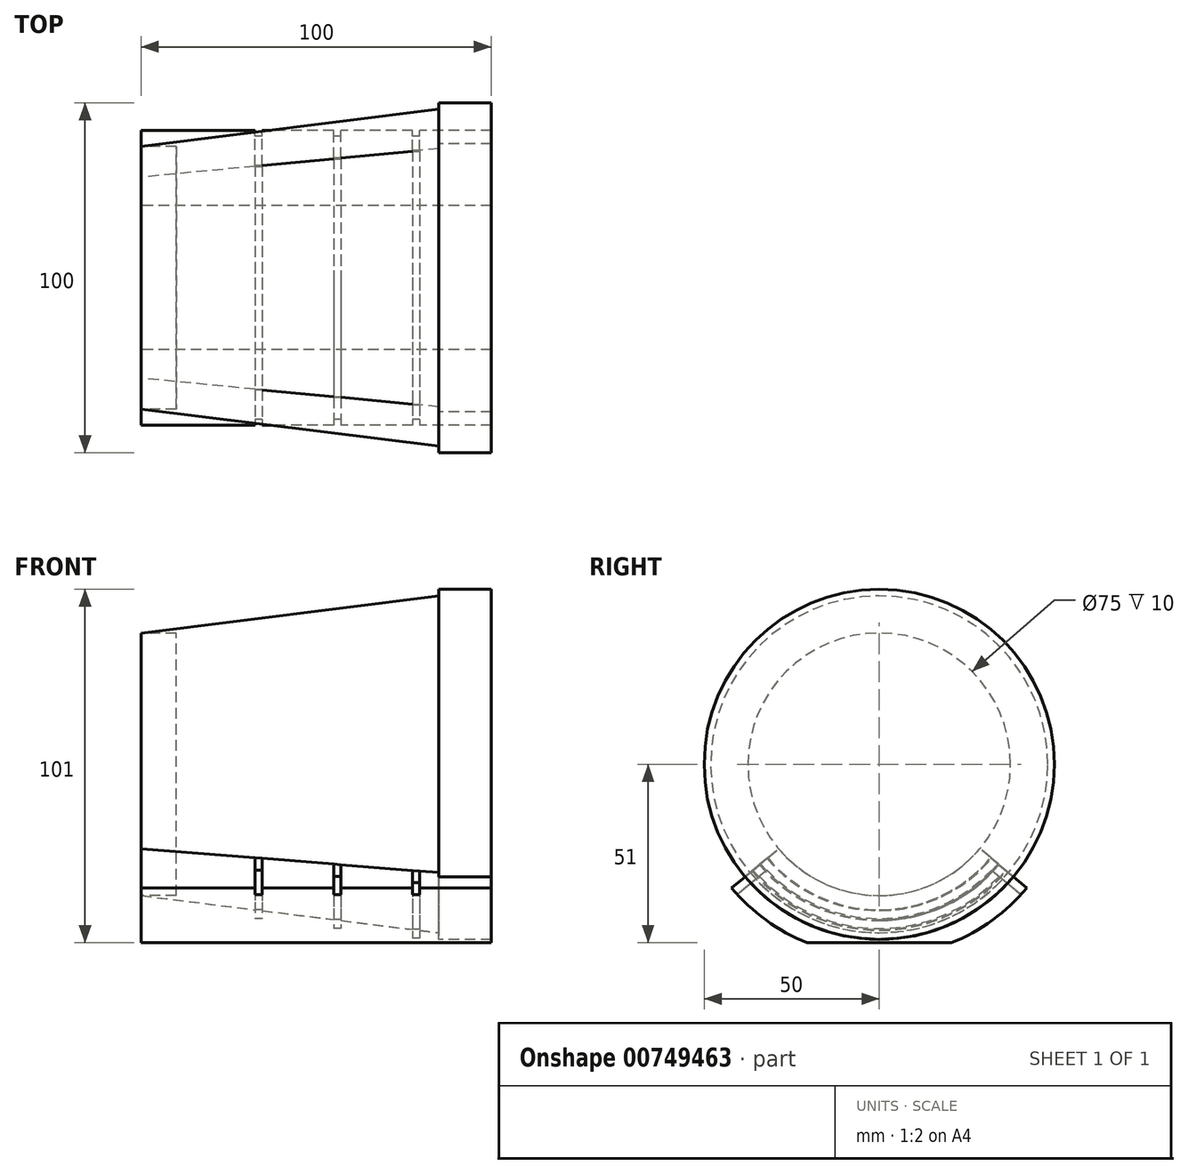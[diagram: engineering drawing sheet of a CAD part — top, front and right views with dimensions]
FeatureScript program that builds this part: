
annotation { "Feature Type Name" : "Feature", "Feature Type Description" : "" }
export const myFeature = defineFeature(function(context is Context, id is Id, definition is map)
    precondition{}
    {
        {
            var Q0;
            Q0=qCreatedBy(makeId("Right.planeOp"),FACE);
            var sketch = newSketch(context, id + "F0", { "sketchPlane" : qUnion([Q0])});
            skCircle(sketch, "E0", {"center": v(0, 0) * mm, "radius": 37.5 * mm});
            skSolve(sketch);
        }
        {
            var Q0;
            Q0=makeQuery(id+"F0.imprint","IMPRINT",FACE,{"disambiguationData":[TD([[makeQuery(id+"F0.imprint","IMPRINT",EDGE,{"derivedFrom":sQuery(id+"F0.wireOp",EDGE,"E0")}),1.0]])]});
            cPlane(context, id + "F1", {"entities" : qUnion([Q0]), "cplaneType" : CPlaneType.OFFSET, "offset" : 100 * mm, "width" : 150 * mm, "height" : 150 * mm});
        }
        {
            var Q0;
            Q0=qCreatedBy(id+"F1.planeOp",FACE);
            var sketch = newSketch(context, id + "F2", { "sketchPlane" : qUnion([Q0])});
            skCircle(sketch, "E1", {"center": v(0, 0) * mm, "radius": 50 * mm});
            skSolve(sketch);
        }
        {
            var Q0;
            Q0=qCreatedBy(id+"F1.planeOp",FACE);
            cPlane(context, id + "F3", {"entities" : qUnion([Q0]), "cplaneType" : CPlaneType.OFFSET, "offset" : 15 * mm, "oppositeDirection" : true, "width" : 150 * mm, "height" : 150 * mm});
        }
        {
            var Q0;
            Q0=qCreatedBy(id+"F3.planeOp",FACE);
            var sketch = newSketch(context, id + "F4", { "sketchPlane" : qUnion([Q0])});
            skCircle(sketch, "E2.0", {"center": v(0, 0) * mm, "radius": 50 * mm});
            skSolve(sketch);
        }
        {
            var Q0;
            Q0=makeQuery(id+"F0.imprint","IMPRINT",FACE,{"disambiguationData":[TD([[makeQuery(id+"F0.imprint","IMPRINT",EDGE,{"derivedFrom":sQuery(id+"F0.wireOp",EDGE,"E0")}),1.0]])]});
            var Q1;
            Q1=makeQuery(id+"F2.imprint","IMPRINT",FACE,{"disambiguationData":[TD([[makeQuery(id+"F2.imprint","IMPRINT",EDGE,{"derivedFrom":sQuery(id+"F2.wireOp",EDGE,"E1")}),1.0]])]});
            loft(context, id + "F5", {"sheetProfilesArray" : [{ "sheetProfileEntities" : qUnion([Q0]) }, { "sheetProfileEntities" : qUnion([Q1]) }]});
        }
        {
            var Q0;
            Q0=makeQuery(id+"F4.imprint","IMPRINT",FACE,{"disambiguationData":[TD([[makeQuery(id+"F4.imprint","IMPRINT",EDGE,{"derivedFrom":sQuery(id+"F4.wireOp",EDGE,"E2.0")}),1.0]])]});
            var Q1;
            Q1=makeQuery(id+"F5.opLoft","CAP_FACE",FACE,{"disambiguationData":[OSD([makeQuery(id+"F2.imprint","IMPRINT",FACE,{"disambiguationData":[TD([[makeQuery(id+"F2.imprint","IMPRINT",EDGE,{"derivedFrom":sQuery(id+"F2.wireOp",EDGE,"E1")}),1.0]])]})])],"isStart":true});
            extrude(context, id + "F6", {"entities" : qUnion([Q0]), "operationType" : NewBodyOperationType.ADD, "endBound" : BoundingType.UP_TO_SURFACE, "depth" : 25 * mm, "endBoundEntityFace" : qUnion([Q1]), "offsetDistance" : 25 * mm});
        }
        {
            var Q0;
            Q0=makeQuery(id+"F5.opLoft","CAP_FACE",FACE,{"disambiguationData":[OSD([makeQuery(id+"F0.imprint","IMPRINT",FACE,{"disambiguationData":[TD([[makeQuery(id+"F0.imprint","IMPRINT",EDGE,{"derivedFrom":sQuery(id+"F0.wireOp",EDGE,"E0")}),1.0]])]})])],"isStart":true});
            extrude(context, id + "F7", {"entities" : qUnion([Q0]), "operationType" : NewBodyOperationType.REMOVE, "oppositeDirection" : true, "depth" : 10 * mm, "offsetDistance" : 25 * mm});
        }
        {
            var Q0;
            Q0=qCreatedBy(makeId("Front.planeOp"),FACE);
            var sketch = newSketch(context, id + "F8", { "sketchPlane" : qUnion([Q0])});
            skLineSegment(sketch, "E3", {"start": v(85, -48.13) * mm, "end": v(0, -37.5) * mm});
            skLineSegment(sketch, "E4", {"start": v(100, -50) * mm, "end": v(85, -50) * mm});
            skLineSegment(sketch, "E5.0", {"start": v(85, -48.13) * mm, "end": v(85, -50) * mm});
            skLineSegment(sketch, "E6.0", {"start": v(100, -48.13) * mm, "end": v(100, -50) * mm});
            skPoint(sketch, "E7.orphan", {"position": v(85, 50) * mm});
            skPoint(sketch, "E8", {"position": v(100, -48.13) * mm});
            skPoint(sketch, "E9.orphan", {"position": v(100, 50) * mm});
            skLineSegment(sketch, "E10", {"start": v(100, -50) * mm, "end": v(100, -55) * mm});
            skLineSegment(sketch, "E11", {"start": v(100, -55) * mm, "end": v(0, -55) * mm});
            skLineSegment(sketch, "E12", {"start": v(0, -55) * mm, "end": v(0, -37.5) * mm});
            skLineSegment(sketch, "E13", {"start": v(0, 0) * mm, "end": v(107.52, 0) * mm, "construction": true});
            skSolve(sketch);
        }
        {
            var Q0;
            Q0=makeQuery(id+"F8.imprint","IMPRINT",FACE,{"disambiguationData":[TD([[makeQuery(id+"F8.imprint","IMPRINT",EDGE,{"derivedFrom":sQuery(id+"F8.wireOp",EDGE,"E3")}),1.0]])]});
            var Q1;
            Q1=sQuery(id+"F8.wireOp",EDGE,"E13");
            revolve(context, id + "F9", {"surfaceOperationType" : NewSurfaceOperationType.NEW, "entities" : qUnion([Q0]), "axis" : qUnion([Q1]), "revolveType" : RevolveType.SYMMETRIC, "angle" : 100 * degree});
        }
        {
            var Q0;
            Q0=makeQuery(id+"F9.opRevolve","CAP_FACE",FACE,{"disambiguationData":[OSD([sQuery(id+"F8.wireOp",EDGE,"E3"),sQuery(id+"F8.wireOp",EDGE,"E4"),sQuery(id+"F8.wireOp",EDGE,"E5.0"),sQuery(id+"F8.wireOp",EDGE,"E10"),sQuery(id+"F8.wireOp",EDGE,"E11"),sQuery(id+"F8.wireOp",EDGE,"E12")])],"isStart":true});
            var sketch = newSketch(context, id + "F10", { "sketchPlane" : qUnion([Q0])});
            skLineSegment(sketch, "E14.bottom", {"start": v(32.5, -41.56) * mm, "end": v(34.5, -41.56) * mm});
            skLineSegment(sketch, "E14.top", {"start": v(32.5, -44.06) * mm, "end": v(34.5, -44.06) * mm});
            skLineSegment(sketch, "E14.left", {"start": v(32.5, -41.56) * mm, "end": v(32.5, -44.06) * mm});
            skLineSegment(sketch, "E14.right", {"start": v(34.5, -41.56) * mm, "end": v(34.5, -44.06) * mm});
            skLineSegment(sketch, "E15.bottom", {"start": v(55, -44.38) * mm, "end": v(57, -44.38) * mm});
            skLineSegment(sketch, "E15.top", {"start": v(55, -46.88) * mm, "end": v(57, -46.88) * mm});
            skLineSegment(sketch, "E15.left", {"start": v(55, -44.38) * mm, "end": v(55, -46.88) * mm});
            skLineSegment(sketch, "E15.right", {"start": v(57, -44.38) * mm, "end": v(57, -46.88) * mm});
            skLineSegment(sketch, "E16.bottom", {"start": v(77.5, -47.19) * mm, "end": v(79.5, -47.19) * mm});
            skLineSegment(sketch, "E16.top", {"start": v(77.5, -49.69) * mm, "end": v(79.5, -49.69) * mm});
            skLineSegment(sketch, "E16.left", {"start": v(77.5, -47.19) * mm, "end": v(77.5, -49.69) * mm});
            skLineSegment(sketch, "E16.right", {"start": v(79.5, -47.19) * mm, "end": v(79.5, -49.69) * mm});
            skSolve(sketch);
        }
        {
            var Q0;
            Q0 = qSketchRegion(id + "F10", true);
            var Q1;
            {var subQ0=sQuery(id+"F10.wireOp",EDGE,"MtueOWO8-KjEm-FWS7-cRDt-SSEm0pxepaqH");Q1=makeQuery(id+"F10.imprint","IMPRINT",FACE,{"disambiguationData":[TD([[makeQuery(id+"F10.imprint","IMPRINT",EDGE,{"derivedFrom":subQ0}),1.0]])]});}
            var Q2;
            {var subQ0=sQuery(id+"F10.wireOp",EDGE,"r30qupwk-UPxA-5DJF-4wcs-cAvNlDd5E6xW");Q2=makeQuery(id+"F10.imprint","IMPRINT",FACE,{"disambiguationData":[TD([[makeQuery(id+"F10.imprint","IMPRINT",EDGE,{"derivedFrom":subQ0}),1.0]])]});}
            var Q3;
            Q3=sQuery(id+"F8.wireOp",EDGE,"E13");
            revolve(context, id + "F11", {"operationType" : NewBodyOperationType.REMOVE, "surfaceOperationType" : NewSurfaceOperationType.NEW, "entities" : qUnion([Q0, Q1, Q2]), "axis" : qUnion([Q3]), "revolveType" : RevolveType.ONE_DIRECTION, "angle" : 100 * degree});
        }
        {
            var Q0;
            Q0=makeQuery(id+"F9.opRevolve","SWEPT_FACE",FACE,{"disambiguationData":[OSD([sQuery(id+"F8.wireOp",EDGE,"E10")])]});
            var sketch = newSketch(context, id + "F12", { "sketchPlane" : qUnion([Q0])});
            skLineSegment(sketch, "E17", {"start": v(0, -50) * mm, "end": v(0, -51) * mm, "construction": true});
            skLineSegment(sketch, "E18", {"start": v(-50.55, -51) * mm, "end": v(49.92, -51) * mm});
            skLineSegment(sketch, "E19", {"start": v(49.92, -51) * mm, "end": v(49.92, -60) * mm});
            skLineSegment(sketch, "E20", {"start": v(49.92, -60) * mm, "end": v(-50.55, -60) * mm});
            skLineSegment(sketch, "E21", {"start": v(-50.55, -60) * mm, "end": v(-50.55, -51) * mm});
            skSolve(sketch);
        }
        {
            var Q0;
            {var subQ0=sQuery(id+"F12.wireOp",EDGE,"E19");Q0=makeQuery(id+"F12.imprint","IMPRINT",FACE,{"disambiguationData":[TD([[makeQuery(id+"F12.imprint","IMPRINT",EDGE,{"derivedFrom":subQ0}),-1.0]])]});}
            var Q1;
            {var subQ0=sQuery(id+"F12.wireOp",EDGE,"E18");var subQ1=makeQuery(id+"F9.opRevolve","SWEPT_EDGE",EDGE,{"disambiguationData":[OSD([sQuery(id+"F8.wireOp",EDGE,"E10"),sQuery(id+"F8.wireOp",EDGE,"E11")])]});var subQ2=makeQuery(id+"F12.imprint","INTERSECT",VERTEX,{"disambiguationData":[OD(0.0)],"derivedFrom":[subQ1,subQ0]});Q1=makeQuery(id+"F12.imprint","IMPRINT",FACE,{"disambiguationData":[TD([[makeQuery(id+"F12.imprint","IMPRINT",EDGE,{"disambiguationData":[TD([[subQ2,-1.0]])],"derivedFrom":subQ0}),-1.0]])]});}
            var Q2;
            Q2=makeQuery(id+"F9.opRevolve","SWEPT_FACE",FACE,{"disambiguationData":[OSD([sQuery(id+"F8.wireOp",EDGE,"E12")])]});
            extrude(context, id + "F13", {"entities" : qUnion([Q0, Q1]), "operationType" : NewBodyOperationType.REMOVE, "endBound" : BoundingType.UP_TO_SURFACE, "oppositeDirection" : true, "depth" : 25 * mm, "endBoundEntityFace" : qUnion([Q2]), "offsetDistance" : 25 * mm});
        }
        {
            var Q0;
            Q0=makeQuery(id+"F9.opRevolve","CAP_FACE",FACE,{"disambiguationData":[OSD([sQuery(id+"F8.wireOp",EDGE,"E3"),sQuery(id+"F8.wireOp",EDGE,"E4"),sQuery(id+"F8.wireOp",EDGE,"E5.0"),sQuery(id+"F8.wireOp",EDGE,"E10"),sQuery(id+"F8.wireOp",EDGE,"E11"),sQuery(id+"F8.wireOp",EDGE,"E12")])],"isStart":true});
            var sketch = newSketch(context, id + "F14", { "sketchPlane" : qUnion([Q0])});
            skLineSegment(sketch, "E22.bottom", {"start": v(32.5, -41.56) * mm, "end": v(34.5, -41.56) * mm});
            skLineSegment(sketch, "E22.top", {"start": v(32.5, -55) * mm, "end": v(34.5, -55) * mm});
            skLineSegment(sketch, "E22.left", {"start": v(32.5, -41.56) * mm, "end": v(32.5, -55) * mm});
            skLineSegment(sketch, "E22.right", {"start": v(34.5, -41.56) * mm, "end": v(34.5, -55) * mm});
            skLineSegment(sketch, "E23.bottom", {"start": v(55, -44.38) * mm, "end": v(57, -44.38) * mm});
            skLineSegment(sketch, "E23.top", {"start": v(55, -55) * mm, "end": v(57, -55) * mm});
            skLineSegment(sketch, "E23.left", {"start": v(55, -44.38) * mm, "end": v(55, -55) * mm});
            skLineSegment(sketch, "E23.right", {"start": v(57, -44.38) * mm, "end": v(57, -55) * mm});
            skLineSegment(sketch, "E24.bottom", {"start": v(77.5, -47.19) * mm, "end": v(79.5, -47.19) * mm});
            skLineSegment(sketch, "E24.top", {"start": v(77.5, -55) * mm, "end": v(79.5, -55) * mm});
            skLineSegment(sketch, "E24.left", {"start": v(77.5, -47.19) * mm, "end": v(77.5, -55) * mm});
            skLineSegment(sketch, "E24.right", {"start": v(79.5, -47.19) * mm, "end": v(79.5, -55) * mm});
            skSolve(sketch);
        }
        {
            var Q0;
            {var subQ0=sQuery(id+"F14.wireOp",EDGE,"E22.top");Q0=makeQuery(id+"F14.imprint","IMPRINT",FACE,{"disambiguationData":[TD([[makeQuery(id+"F14.imprint","IMPRINT",EDGE,{"derivedFrom":subQ0}),-1.0]])]});}
            var Q1;
            {var subQ8=sQuery(id+"F14.wireOp",EDGE,"E22.bottom");Q1=makeQuery(id+"F14.imprint","IMPRINT",FACE,{"disambiguationData":[TD([[makeQuery(id+"F14.imprint","IMPRINT",EDGE,{"derivedFrom":subQ8}),-1.0]])]});}
            var Q2;
            {var subQ7=sQuery(id+"F14.wireOp",EDGE,"E23.bottom");Q2=makeQuery(id+"F14.imprint","IMPRINT",FACE,{"disambiguationData":[TD([[makeQuery(id+"F14.imprint","IMPRINT",EDGE,{"derivedFrom":subQ7}),-1.0]])]});}
            var Q3;
            {var subQ0=sQuery(id+"F14.wireOp",EDGE,"E23.top");Q3=makeQuery(id+"F14.imprint","IMPRINT",FACE,{"disambiguationData":[TD([[makeQuery(id+"F14.imprint","IMPRINT",EDGE,{"derivedFrom":subQ0}),-1.0]])]});}
            var Q4;
            {var subQ8=sQuery(id+"F14.wireOp",EDGE,"E24.bottom");Q4=makeQuery(id+"F14.imprint","IMPRINT",FACE,{"disambiguationData":[TD([[makeQuery(id+"F14.imprint","IMPRINT",EDGE,{"derivedFrom":subQ8}),-1.0]])]});}
            var Q5;
            {var subQ0=sQuery(id+"F14.wireOp",EDGE,"E24.top");Q5=makeQuery(id+"F14.imprint","IMPRINT",FACE,{"disambiguationData":[TD([[makeQuery(id+"F14.imprint","IMPRINT",EDGE,{"derivedFrom":subQ0}),-1.0]])]});}
            extrude(context, id + "F15", {"entities" : qUnion([Q0, Q1, Q2, Q3, Q4, Q5]), "operationType" : NewBodyOperationType.REMOVE, "oppositeDirection" : true, "depth" : 2.5 * mm, "offsetDistance" : 25 * mm});
        }
        {
            var Q0;
            Q0=makeQuery(id+"F9.opRevolve","CAP_FACE",FACE,{"disambiguationData":[OSD([sQuery(id+"F8.wireOp",EDGE,"E3"),sQuery(id+"F8.wireOp",EDGE,"E4"),sQuery(id+"F8.wireOp",EDGE,"E5.0"),sQuery(id+"F8.wireOp",EDGE,"E10"),sQuery(id+"F8.wireOp",EDGE,"E11"),sQuery(id+"F8.wireOp",EDGE,"E12")])],"isStart":false});
            var sketch = newSketch(context, id + "F16", { "sketchPlane" : qUnion([Q0])});
            skLineSegment(sketch, "E25.bottom", {"start": v(32.5, 41.56) * mm, "end": v(34.5, 41.56) * mm});
            skLineSegment(sketch, "E25.top", {"start": v(32.5, 55) * mm, "end": v(34.5, 55) * mm});
            skLineSegment(sketch, "E25.left", {"start": v(32.5, 41.56) * mm, "end": v(32.5, 55) * mm});
            skLineSegment(sketch, "E25.right", {"start": v(34.5, 41.56) * mm, "end": v(34.5, 55) * mm});
            skLineSegment(sketch, "E26.bottom", {"start": v(55, 44.38) * mm, "end": v(57, 44.38) * mm});
            skLineSegment(sketch, "E26.top", {"start": v(55, 55) * mm, "end": v(57, 55) * mm});
            skLineSegment(sketch, "E26.left", {"start": v(55, 44.38) * mm, "end": v(55, 55) * mm});
            skLineSegment(sketch, "E26.right", {"start": v(57, 44.38) * mm, "end": v(57, 55) * mm});
            skLineSegment(sketch, "E27.bottom", {"start": v(77.5, 47.19) * mm, "end": v(79.5, 47.19) * mm});
            skLineSegment(sketch, "E27.top", {"start": v(77.5, 55) * mm, "end": v(79.5, 55) * mm});
            skLineSegment(sketch, "E27.left", {"start": v(77.5, 47.19) * mm, "end": v(77.5, 55) * mm});
            skLineSegment(sketch, "E27.right", {"start": v(79.5, 47.19) * mm, "end": v(79.5, 55) * mm});
            skSolve(sketch);
        }
        {
            var Q0;
            {var subQ0=sQuery(id+"F16.wireOp",EDGE,"E27.top");Q0=makeQuery(id+"F16.imprint","IMPRINT",FACE,{"disambiguationData":[TD([[makeQuery(id+"F16.imprint","IMPRINT",EDGE,{"derivedFrom":subQ0}),1.0]])]});}
            var Q1;
            {var subQ8=sQuery(id+"F16.wireOp",EDGE,"E27.bottom");Q1=makeQuery(id+"F16.imprint","IMPRINT",FACE,{"disambiguationData":[TD([[makeQuery(id+"F16.imprint","IMPRINT",EDGE,{"derivedFrom":subQ8}),1.0]])]});}
            var Q2;
            {var subQ7=sQuery(id+"F16.wireOp",EDGE,"E26.bottom");Q2=makeQuery(id+"F16.imprint","IMPRINT",FACE,{"disambiguationData":[TD([[makeQuery(id+"F16.imprint","IMPRINT",EDGE,{"derivedFrom":subQ7}),1.0]])]});}
            var Q3;
            {var subQ0=sQuery(id+"F16.wireOp",EDGE,"E26.top");Q3=makeQuery(id+"F16.imprint","IMPRINT",FACE,{"disambiguationData":[TD([[makeQuery(id+"F16.imprint","IMPRINT",EDGE,{"derivedFrom":subQ0}),1.0]])]});}
            var Q4;
            {var subQ0=sQuery(id+"F16.wireOp",EDGE,"E25.top");Q4=makeQuery(id+"F16.imprint","IMPRINT",FACE,{"disambiguationData":[TD([[makeQuery(id+"F16.imprint","IMPRINT",EDGE,{"derivedFrom":subQ0}),1.0]])]});}
            var Q5;
            {var subQ8=sQuery(id+"F16.wireOp",EDGE,"E25.bottom");Q5=makeQuery(id+"F16.imprint","IMPRINT",FACE,{"disambiguationData":[TD([[makeQuery(id+"F16.imprint","IMPRINT",EDGE,{"derivedFrom":subQ8}),1.0]])]});}
            extrude(context, id + "F17", {"entities" : qUnion([Q0, Q1, Q2, Q3, Q4, Q5]), "operationType" : NewBodyOperationType.REMOVE, "oppositeDirection" : true, "depth" : 2.5 * mm, "offsetDistance" : 25 * mm});
        }
    });
